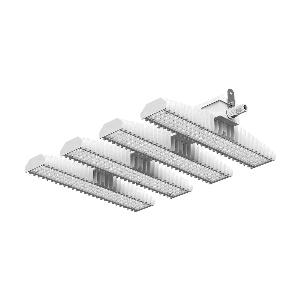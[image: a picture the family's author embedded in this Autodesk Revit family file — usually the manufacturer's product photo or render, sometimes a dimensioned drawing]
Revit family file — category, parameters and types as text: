
# Revit family: 3f_filippi_-_3f_lem_concentrato_3f_filippi_-_58908_-_3f_lem_4_led_200_dali_cr_conc
name_source: partatom
category: Lighting Fixtures
units: mm (PartAtom-declared; Revit-internal decimal feet)

## family parameters
Cut with Voids When Loaded = No
Host = Face
Light Source = No
Part Type = Normal
Room Calculation Point = No
Round Connector Dimension = Use Diameter
Shared = No

## types (1)
- 3F Filippi - 3F LEM Concentrato (1 x LED, 32540 lm, 218 W, 4000 K)
    Apparent Load = 218 VA
    Approval mark = CE
    CIE Flux Codes = 83 96 99 100 100
    Color Rendering = 80
    Color Temperature = 4000 K
    Control Gear = Electronic transformer
    Default Elevation = 1800 mm
    Description = Industrial luminaire with high light output and high luminous efficiency designed with the most innovative technologies for environments with temperature up to 55°C.

ILLUMINOTECHNICAL
Luminous efficiency 100% (DLOR 100%, ULOR 0%).
Initial luminous flux of the luminaire 32540 lm.
Direct symmetric narrow distribution: the illuminated area has a elliptical shape.
Installation Interdistance Transv.D = 0.52 x hu - Long.D = 1.16 x hu.
Tabular UGR (CIE 117 - 4H-8H; S=0.25H; 70/50/20): RUG 17.5 - 21.3.
Beam angle: 31° - 73°.
Luminous efficacy 149 lm/W.
Lifetime (L93/B10): 30000 h. (tq+25°C)
Lifetime (L90/B10): 50000 h. (tq+25°C)
Lifetime (L85/B10): 80000 h. (tq+25°C)
Lifetime (L80/B10): 100000 h. (tq+25°C)
Lifetime (L85/B10): 50000 h. (tq+55°C)
Sudden decreased luminous flux after 50000 hours: 0% (C0).
Photobiological safety in compliance with IEC/TR 62778: RG0 risk exempt, (IEC 62471).
In compliance with IEC/EN 62722-2-1 - IEC/EN 62717 standards.

SOURCE
4 Mid-Power linear LED modules 50W/840.
Energy efficiency class (UE 2019/2020 - UE 2019/2015): C.
CIE 13.3 Colour rendering index: CRI >80 (R9 <50%).
IES TM-30 Fidelity Index: Rf = 84 Rg = 95.
CCT nominal colour temperature 4000 K.
Colour initial tolerance (MacAdam): SDCM 3.

MECHANICAL
Passive modular heatsinks in die-casted aluminium, painted in white colour.
To optimize the thermal management of the LED module, the heatsinks are oversized and provided with self-cleaning of cooling fins.
Wiring body in aluminium and galvanised steel anchored solidly to the sinks and thermally separated.
3F Lens lenses with high luminous efficiency, transparent methacrylate (PMMA), fixed to the LED modules.
Fixing brackets in stainless steel.
Luminaire with limited surface temperature. - D - (EN 60598-2-24)
Dimensions: 757x542 mm, height 129 mm. Weight 16.7 kg.
IP65 protection degree.
Mechanical strength to impacts IK06 (1 joule).
Glow-wire test resistance 650°C.

ELECTRICAL
Halogen Free DALI-2 DATI (Parts 251, 252, 253), PUSH-DIM, electronic wiring 230V-50/60Hz, power factor 0.97 at full load, THD <25%, constant output current, class I, 2 driver, 2 DALI addresses.
Power of the luminaire 218 W.
ENEC - CE.
Flicker: <4%.
Luminaire compliant with EN 60598-2-22 for power supply from a centralised emergency system CPSS (Central Power Supply System), not incorporated in the luminaire - high risk areas excluded. The default power and flux are 100% in AC and 15% in DC.
Ambient temperature from -30°C to +55°C.
Temperature class T6 max 85°C.
Quick connection via M25 5P connector with 9-13 mm tightening range.
Power unit positioned on a separate compartment by the LED module to ensure optimum temperatures of cabling components, to be inspectable and maintainable.
Relative humidity UR: <85%.

INSTALLATION
Ceiling / Suspended / Wall.
All accessories dedicated to this product are available on the Catalog and on our website www.3F-Filippi.com.

APPLICATIONS
In commercial environments, exhibition and industrial areas, stores, open areas or with shelves.
Applications with high ambient temperature up to 55°C.
Environments in which it is necessary a total protection against falling fragments (eg environments with foodstuffs or machines with moving parts or with extreme temperature changes), use luminaires with polycarbonate lenses.

LIGHT MANAGEMENT
Recommended minimum setting: 10%.
The luminaire, equipped with (DALI-2 DATI) driver, can be controlled manually with 3F Easy Dim technology or automatically/manually with wired or wireless DALI/D2D control systems.
The D2D driver guarantees interoperability with other devices with the same certification by making the following information available:
Device Data (Part 251), Energy Report (Part 252), Diagnosis & Maintenance (Part 253).
In electrical systems without a regulation system (manual or automatic) and DALI bus, a suitable jumper must be made on the DA-DA terminals of the appliance.

WARNING
Fixture not suitable for cold stores with an ambient temperature <0°C and/or relative humidity >85%.
Luminaire designed for disposal/recycling at end-of-life.
Replaceable (LED only) light source by a professional. Replaceable control gear by a professional.
    Height = 129 mm
    Lamp = 1 x LED
    Lamp Light Flux = 32540 lm
    Lamp Power = 218 W
    Lamp count = 1
    Length = 757 mm
    Lifetime = 50000 h
    Luminous efficacy = 149 lm/W
    Manufacturer = 3F Filippi
    ModVariant = No
    Model = 3F Filippi - 58908 - 3F LEM 4 LED 200 DALI CR CONC
    Mounting Place = Ceiling
    Mounting Type = Pendant
    Number of Poles = 1
    OnlyDefault = Yes
    Power Factor = 1
    Product Name = 3F Filippi - 3F LEM Concentrato
    Product group = pendant luminaire
    ProductGroupID = 9
    Protection Class = Protection class I
    Protection Degree = IP 65
    RLX_Detail_Level = 1
    RLX_Emergency_Light_Flux = 0 lm
    RLX_Emergency_Type = 0
    RLX_Emergency_Type_DB = No
    RlxData = <blob elided: 118481 chars, md5=279e2b0a>
    Socket = socket
    Standby Power = 0 W
    System Light Flux = 32540 lm
    System Power = 218 W
    Type Comments = Product without accessories
    Type Image = 3f_filippi_-_lem_4.jpg
    URL = http://relux.com
    VarID = ---
    Voltage = 0 V
    Weight = 0.00 kg
    Width = 542 mm

## geometry (parser evidence)
native form markers: Blend x4, Sweep x14
no freeform markers — native parametric forms only
